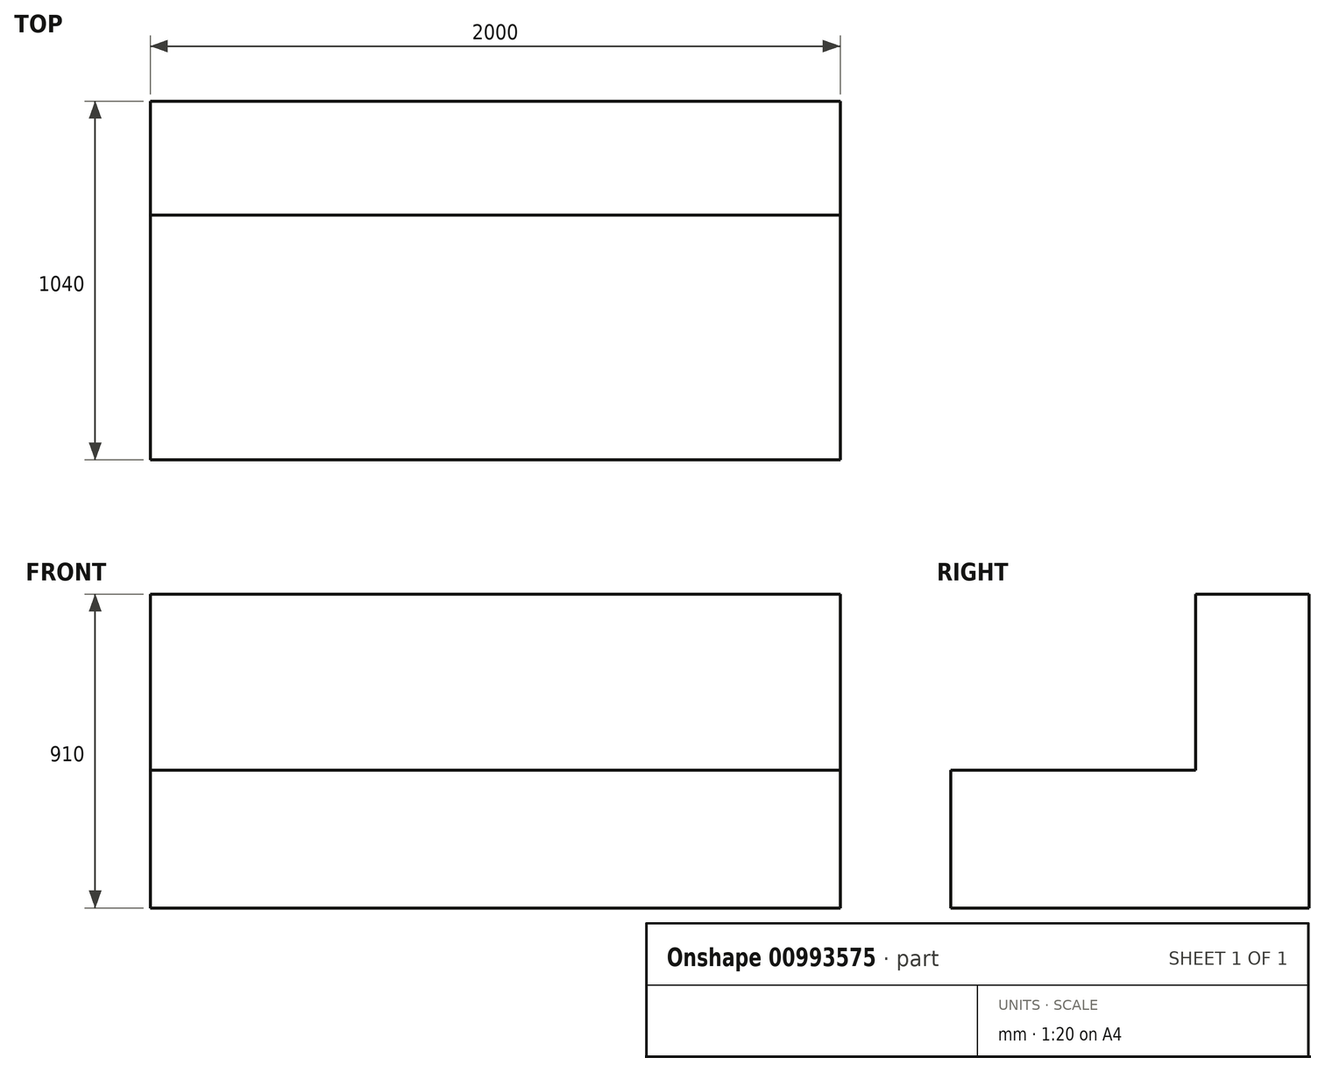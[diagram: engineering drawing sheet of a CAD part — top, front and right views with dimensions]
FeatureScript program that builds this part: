
annotation { "Feature Type Name" : "Feature", "Feature Type Description" : "" }
export const myFeature = defineFeature(function(context is Context, id is Id, definition is map)
    precondition{}
    {
        {
            var Q0;
            Q0=qCreatedBy(makeId("Right.planeOp"),FACE);
            var sketch = newSketch(context, id + "F0", { "sketchPlane" : qUnion([Q0])});
            skLineSegment(sketch, "E0", {"start": v(0, 0) * mm, "end": v(0, 910) * mm});
            skLineSegment(sketch, "E1", {"start": v(0, 910) * mm, "end": v(-330, 910) * mm});
            skLineSegment(sketch, "E2", {"start": v(-330, 910) * mm, "end": v(-330, 400) * mm});
            skLineSegment(sketch, "E3", {"start": v(-330, 400) * mm, "end": v(-1040, 400) * mm});
            skLineSegment(sketch, "E4", {"start": v(-1040, 400) * mm, "end": v(-1040, 0) * mm});
            skLineSegment(sketch, "E5", {"start": v(-1040, 0) * mm, "end": v(0, 0) * mm});
            skSolve(sketch);
        }
        {
            var Q0;
            Q0 = qSketchRegion(id + "F0", true);
            extrude(context, id + "F1", {"entities" : qUnion([Q0]), "endBound" : BoundingType.SYMMETRIC, "depth" : 2000 * mm, "offsetDistance" : 25 * mm});
        }
    });
